# Revit family: Allermuir_Pinn_UK_Rvt23
name_source: partatom
category: Furniture
units: mm (PartAtom-declared; Revit-internal decimal feet)

## family parameters
Always vertical = Yes
Cut with Voids When Loaded = No
Enable Cutting in Views = No
OmniClass Number = 23.40.20.00
OmniClass Title = General Furniture and Specialties
Render Appearance Source = Family Geometry
Room Calculation Point = No
Shared = No
Work Plane-Based = No

## types (1)
- PINNAL
    Assembly Code = E2020200
    AssetType = Moveable
    BIMObjectName = Allermuir Pinn UK
    Category = Pr_70_70_48_32
    Default Elevation = 0 mm  [stored 0 ft]
    Description = Pinn
    DurationUnit = year
    Export Type to IFC As = IfcFurnitureType
    Features = Has 3 Stage touch dimmable. 180lm output at max brightness & 2700k colour temperature. Come with USB-C Charging (cable incuded) 10hr battery life, 6hr charging time. IP44 rated (splashproof).
    FramesFinish = Powder Coat
    FramesFinishOptions = Tobacco, Ercu
    FramesMaterial = Aluminum
    IfcExportAs = IfcFurnitureType
    IfcExportType = USERDEFINED
    IsBuiltIn = No
    Manufacturer = Allermuir
    ManufacturerName = Allermuir
    ManufacturerURL = https://www.allermuir.com
    Material = Aluminium
    Model = PINNAL
    ModelNumber = PINNAL
    ModelReference = Pinn
    NBSDescription = Free Standing Luminaires
    NBSReference = 90-60-50/405
    NominalDepth = 160 mm  [stored 0.524934 ft]
    NominalHeight = 205 mm  [stored 0.672572 ft]
    NominalWidth = 160 mm  [stored 0.524934 ft]
    Overall Depth = 161 mm
    Overall Height = 201 mm
    Overall Width = 161 mm
    ProductInformation = https://www.allermuir.com
    Revision = 0
    Size = 160.0mm (W) x 160.0mm (D) x 201.0mm (H)
    Status = UNSET
    Type IFC Predefined Type = USERDEFINED
    URL = https://www.allermuir.com
    Uniclass2015Code = Pr_70_70_48_32
    Uniclass2015Title = Free Standing Luminaires
    Uniclass2015Version = Products v1.9
    Version = 1
    WarrantyDescription = Allermuir warrant that its manufactured products are free from manufacturing defects - in materials or workmanship - for a period of ten (10) years. Allermuir will repair, or replace (at Allermuir's sole discretion) with comparable free of charge materials / components, any product / component which fails under normal use in a single shift environment, as a result of a defect in the materials and/ or workmanship.
    WarrantyDurationParts = 10
    WarrantyDurationUnit = year
    Weight = 0.80 kg

note: [stored X ft] marks values corroborated as IEEE doubles in the binary element streams (Revit-internal decimal feet)

## geometry (parser evidence)
native form markers: Sweep x2
no freeform markers — native parametric forms only
